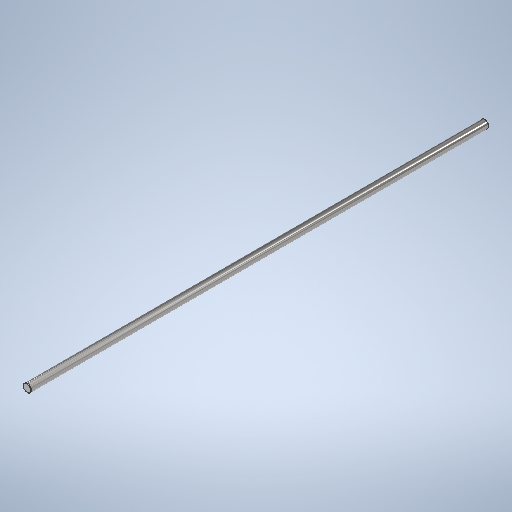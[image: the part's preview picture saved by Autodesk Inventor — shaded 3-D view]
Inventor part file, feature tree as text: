
AUTODESK INVENTOR PART (.ipt)
format: ipt  version: 2025.2 (Build 292293000, 293)  size: 254,464 bytes
history: native  units: mm
features: extrude x1, chamfer x1, sketch x1
ambient origin geometry x8: Origin, YZ Plane, XZ Plane, XY Plane, X Axis, Y Axis, Z Axis, Center Point
bodies: Solid1 (feature_tree)
feature tree (3):
  extrude  "Extrusion1"  Depth=450.0mm TaperAngle=0.0deg
  chamfer  "Chamfer1"  Distance=0.5mm Angle=45.0deg
  sketch  "Sketch1"  dims[d0=8.0mm d1=450.0mm d2=0.0mm d3=0.5mm d4=2.0mm d5=45.0deg]
